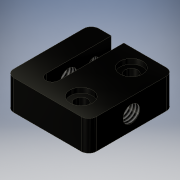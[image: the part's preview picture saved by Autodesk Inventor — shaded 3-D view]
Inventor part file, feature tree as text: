
AUTODESK INVENTOR PART (.ipt)
format: ipt  version: 2019 (Build 230136000, 136)  size: 183,808 bytes
history: native  units: mm
features: sketch x4, extrude x3, hole x2
ambient origin geometry x8: Origin, YZ Plane, XZ Plane, XY Plane, X Axis, Y Axis, Z Axis, Center Point
bodies: Solid1 (feature_tree)
feature tree (9):
  extrude  "Extrusion1"  Depth=34.0mm
  sketch  "Sketch2"  dims[d2=5.0mm d3=26.0mm d4=28.0mm]
  hole  "Hole1"  [1 undecoded]
  hole  "Hole2"  [1 undecoded]
  extrude  "Extrusion2"  Depth=20.0mm
  extrude  "Extrusion3"  Depth=10.0mm
  sketch  "Sketch1"  dims[d0=33.0mm d1=34.0mm]
  sketch  "Sketch3"  dims[d5=8.0mm d6=5.0mm]
  sketch  "Sketch4"  dims[d7=5.0mm d8=20.0mm d9=10.0mm d10=7.0mm d11=3.04mm d12=12.0mm d13=0.0mm d14=8.0mm d15=5.0mm d16=6.0mm d17=10.0mm d18=6.647mm d19=40.0mm d20=9.0mm d21=2.0mm d22=90.0deg d23=40.0mm d24=20.594885mm d25=4.134mm d26=10.0mm d27=9.0mm d28=2.0mm d29=90.0deg d30=10.0mm d31=20.594885mm d32=9.0mm d33=9.0mm d34=2.0mm d35=0.0mm d36=8.0mm d37=8.0mm d38=5.0mm d39=0.0mm]
note: 2 required parameter values undecoded (feature->parameter linkage not recoverable at this tier; creation-order binding heuristic only, values carry confidence <= 0.55)
